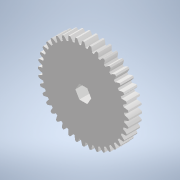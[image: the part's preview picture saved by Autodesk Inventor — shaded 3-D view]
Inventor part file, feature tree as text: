
AUTODESK INVENTOR PART (.ipt)
format: ipt  version: 2022 (Build 260153000, 153)  size: 2,207,232 bytes
history: native  units: mm
features: extrude x2, sketch x2
ambient origin geometry x8: Origin, YZ Plane, XZ Plane, XY Plane, X Axis, Y Axis, Z Axis, Center Point
bodies: Solid1 (feature_tree)
feature tree (4):
  extrude  "Extrusion1"  Depth=6.2mm
  extrude  "Extrusion2"  Depth=6.2mm TaperAngle=0.0deg
  sketch  "Sketch4"  dims[d5=6.2mm d6=0.0mm d7=3.1mm]
  sketch  "Sketch5"  dims[d8=60.0mm d10=360.0deg d12=6.2mm d13=0.0mm d14=0.5mm]
